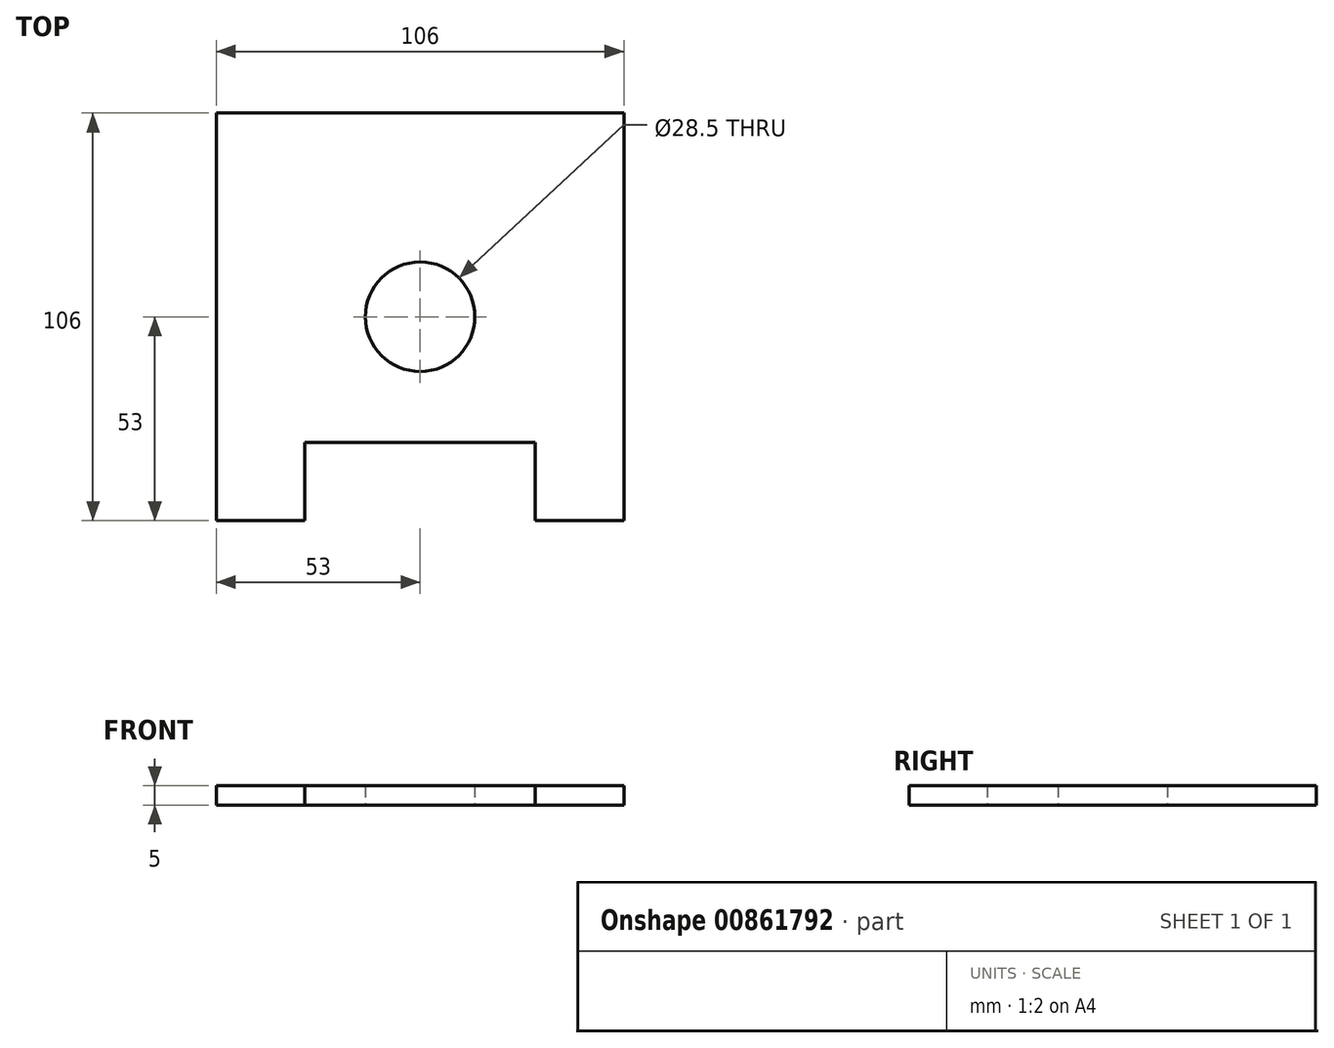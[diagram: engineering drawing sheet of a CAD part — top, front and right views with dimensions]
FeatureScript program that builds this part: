
annotation { "Feature Type Name" : "Feature", "Feature Type Description" : "" }
export const myFeature = defineFeature(function(context is Context, id is Id, definition is map)
    precondition{}
    {
        {
            var Q0;
            Q0=qCreatedBy(makeId("Top.planeOp"),FACE);
            var sketch = newSketch(context, id + "F0", { "sketchPlane" : qUnion([Q0])});
            skLineSegment(sketch, "E0.top", {"start": v(53, 53) * mm, "end": v(-53, 53) * mm});
            skLineSegment(sketch, "E0.left", {"start": v(53, -53) * mm, "end": v(53, 53) * mm});
            skLineSegment(sketch, "E0.right", {"start": v(-53, -53) * mm, "end": v(-53, 53) * mm});
            skPoint(sketch, "E0.middle", {"position": v(0, 0) * mm});
            skCircle(sketch, "E1", {"center": v(0, 0) * mm, "radius": 14.25 * mm});
            skLineSegment(sketch, "E2.top", {"start": v(-30, -32.67) * mm, "end": v(30, -32.67) * mm});
            skLineSegment(sketch, "E2.left", {"start": v(-30, -53) * mm, "end": v(-30, -32.67) * mm});
            skLineSegment(sketch, "E2.right", {"start": v(30, -53) * mm, "end": v(30, -32.67) * mm});
            skLineSegment(sketch, "E3", {"start": v(-53, -53) * mm, "end": v(-30, -53) * mm});
            skLineSegment(sketch, "E4", {"start": v(30, -53) * mm, "end": v(53, -53) * mm});
            skSolve(sketch);
        }
        {
            var Q0;
            Q0=makeQuery(id+"F0.imprint","IMPRINT",FACE,{"disambiguationData":[TD([[makeQuery(id+"F0.imprint","IMPRINT",EDGE,{"derivedFrom":sQuery(id+"F0.wireOp",EDGE,"E0.top")}),1.0]])]});
            extrude(context, id + "F1", {"entities" : qUnion([Q0]), "depth" : 5 * mm, "offsetDistance" : 25 * mm});
        }
    });
